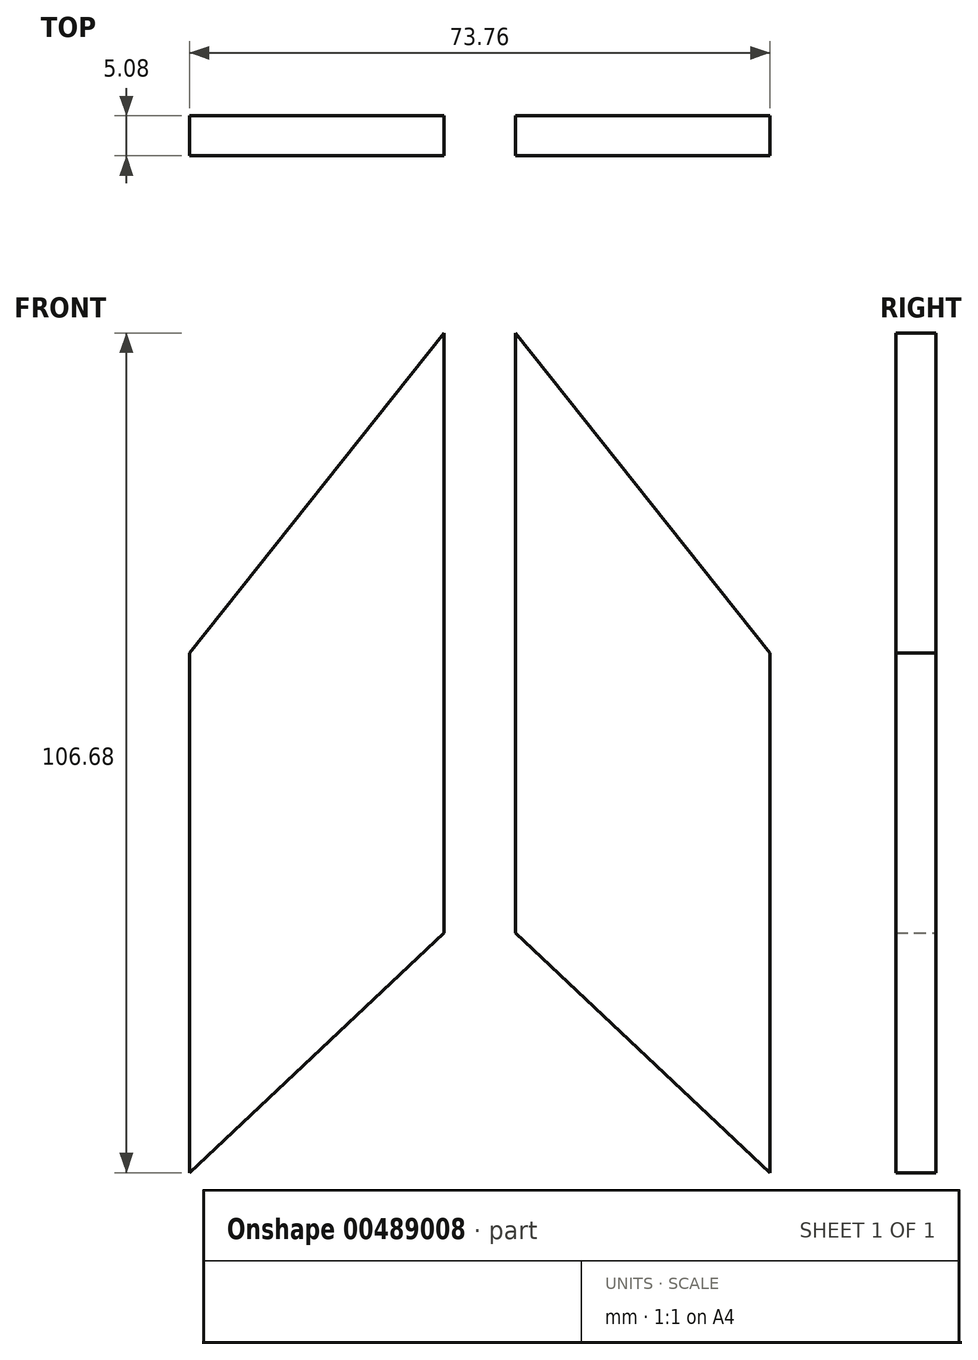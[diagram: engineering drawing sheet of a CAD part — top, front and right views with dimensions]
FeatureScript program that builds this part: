
annotation { "Feature Type Name" : "Feature", "Feature Type Description" : "" }
export const myFeature = defineFeature(function(context is Context, id is Id, definition is map)
    precondition{}
    {
        {
            var Q0;
            Q0=qCreatedBy(makeId("Front.planeOp"),FACE);
            var sketch = newSketch(context, id + "F0", { "sketchPlane" : qUnion([Q0])});
            skLineSegment(sketch, "E0", {"start": v(0, 40.64) * mm, "end": v(32.35, 0) * mm});
            skLineSegment(sketch, "E1", {"start": v(32.35, 0) * mm, "end": v(32.35, -66.04) * mm});
            skLineSegment(sketch, "E2", {"start": v(32.35, -66.04) * mm, "end": v(0, -35.56) * mm});
            skLineSegment(sketch, "E3", {"start": v(0, -35.56) * mm, "end": v(0, 40.64) * mm});
            skLineSegment(sketch, "E4", {"start": v(-9.06, 40.64) * mm, "end": v(-9.06, -35.56) * mm});
            skLineSegment(sketch, "E5", {"start": v(-9.06, -35.56) * mm, "end": v(-41.4, -66.04) * mm});
            skLineSegment(sketch, "E6", {"start": v(-41.4, -66.04) * mm, "end": v(-41.4, 0) * mm});
            skLineSegment(sketch, "E7", {"start": v(-41.4, 0) * mm, "end": v(-9.06, 40.64) * mm});
            skSolve(sketch);
        }
        {
            var Q0;
            Q0=makeQuery(id+"F0.imprint","IMPRINT",FACE,{"disambiguationData":[TD([[makeQuery(id+"F0.imprint","IMPRINT",EDGE,{"derivedFrom":sQuery(id+"F0.wireOp",EDGE,"E0")}),-1.0]])]});
            var Q1;
            Q1=makeQuery(id+"F0.imprint","IMPRINT",FACE,{"disambiguationData":[TD([[makeQuery(id+"F0.imprint","IMPRINT",EDGE,{"derivedFrom":sQuery(id+"F0.wireOp",EDGE,"E4")}),-1.0]])]});
            extrude(context, id + "F1", {"entities" : qUnion([Q0, Q1]), "depth" : 5.08 * mm});
        }
    });
